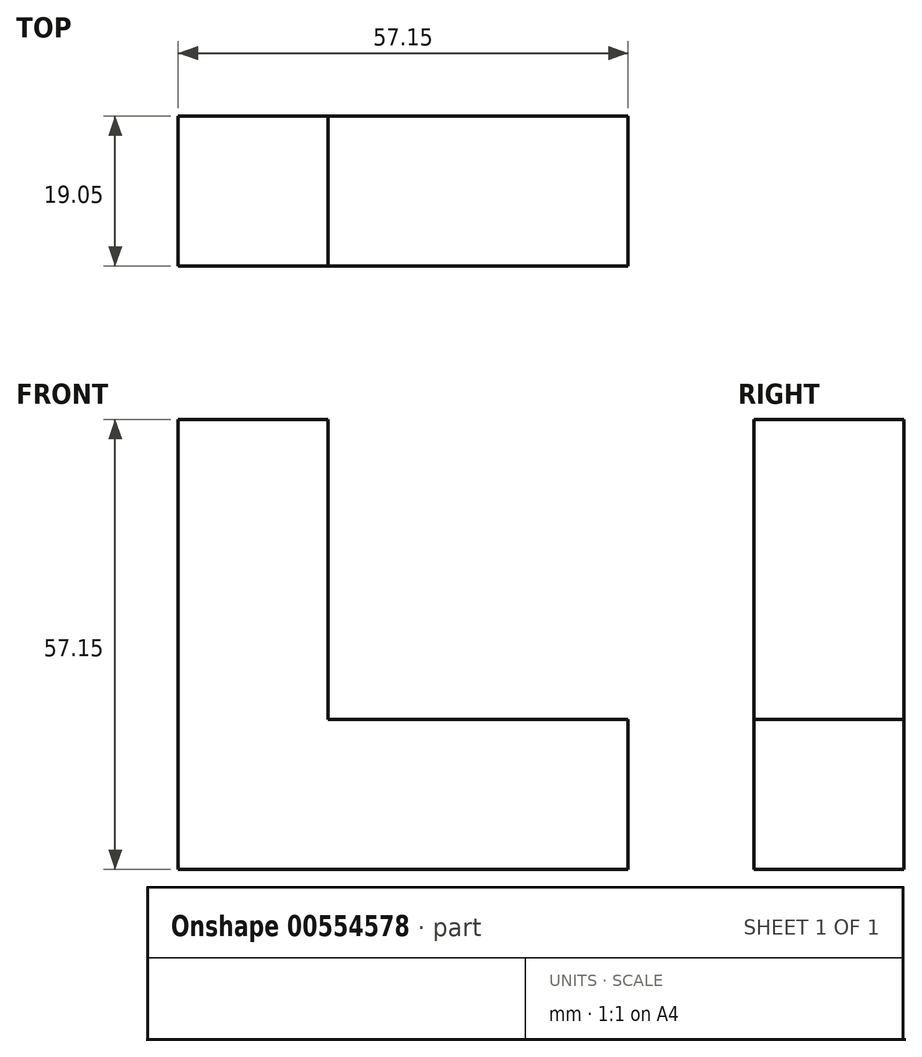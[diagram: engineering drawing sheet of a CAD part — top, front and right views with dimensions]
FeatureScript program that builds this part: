
annotation { "Feature Type Name" : "Feature", "Feature Type Description" : "" }
export const myFeature = defineFeature(function(context is Context, id is Id, definition is map)
    precondition{}
    {
        {
            var Q0;
            Q0=qCreatedBy(makeId("Front.planeOp"),FACE);
            var sketch = newSketch(context, id + "F0", { "sketchPlane" : qUnion([Q0])});
            skLineSegment(sketch, "E0", {"start": v(-66.1, 8.92) * mm, "end": v(-66.1, -48.23) * mm});
            skLineSegment(sketch, "E1", {"start": v(-66.1, -48.23) * mm, "end": v(-8.96, -48.23) * mm});
            skLineSegment(sketch, "E2", {"start": v(-8.96, -48.23) * mm, "end": v(-8.96, -29.18) * mm});
            skLineSegment(sketch, "E3", {"start": v(-8.96, -29.18) * mm, "end": v(-47.06, -29.18) * mm});
            skLineSegment(sketch, "E4", {"start": v(-47.06, -29.18) * mm, "end": v(-47.06, 8.92) * mm});
            skLineSegment(sketch, "E5", {"start": v(-47.06, 8.92) * mm, "end": v(-66.1, 8.92) * mm});
            skSolve(sketch);
        }
        {
            var Q0;
            Q0 = qSketchRegion(id + "F0", true);
            extrude(context, id + "F1", {"entities" : qUnion([Q0]), "depth" : 19.05 * mm, "offsetDistance" : 25.4 * mm});
        }
    });
